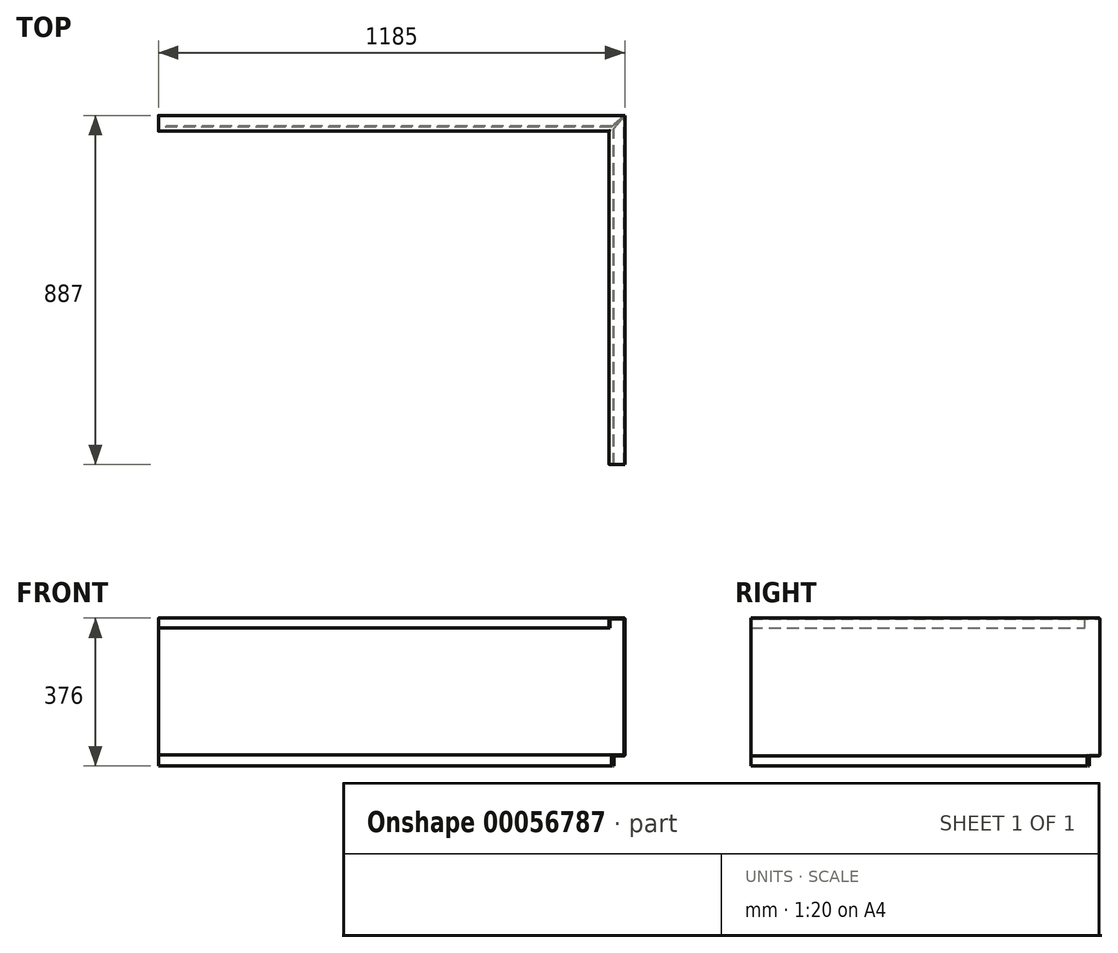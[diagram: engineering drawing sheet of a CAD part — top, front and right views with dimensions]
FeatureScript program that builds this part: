
annotation { "Feature Type Name" : "Feature", "Feature Type Description" : "" }
export const myFeature = defineFeature(function(context is Context, id is Id, definition is map)
    precondition{}
    {
        {
            var Q0;
            Q0=qCreatedBy(makeId("Front.planeOp"),FACE);
            var sketch = newSketch(context, id + "F0", { "sketchPlane" : qUnion([Q0])});
            skLineSegment(sketch, "E0", {"start": v(0, 0) * mm, "end": v(0, -350) * mm});
            skLineSegment(sketch, "E1", {"start": v(0, -350) * mm, "end": v(-27, -350) * mm});
            skLineSegment(sketch, "E2", {"start": v(-27, -350) * mm, "end": v(-27, -376) * mm});
            skLineSegment(sketch, "E3", {"start": v(0, 0) * mm, "end": v(-40, 0) * mm});
            skLineSegment(sketch, "E4", {"start": v(-40, 0) * mm, "end": v(-40, -25) * mm});
            skLineSegment(sketch, "E5.0", {"start": v(-38, -2) * mm, "end": v(-38, -25) * mm});
            skLineSegment(sketch, "E5.1", {"start": v(-29, -348) * mm, "end": v(-29, -376) * mm});
            skLineSegment(sketch, "E5.2", {"start": v(-2, -348) * mm, "end": v(-29, -348) * mm});
            skLineSegment(sketch, "E5.3", {"start": v(-2, -2) * mm, "end": v(-2, -348) * mm});
            skLineSegment(sketch, "E5.4", {"start": v(-2, -2) * mm, "end": v(-38, -2) * mm});
            skLineSegment(sketch, "E6", {"start": v(-40, -25) * mm, "end": v(-38, -25) * mm});
            skLineSegment(sketch, "E7", {"start": v(-29, -376) * mm, "end": v(-27, -376) * mm});
            skSolve(sketch);
        }
        {
            var Q0;
            Q0=qCreatedBy(makeId("Top.planeOp"),FACE);
            var sketch = newSketch(context, id + "F1", { "sketchPlane" : qUnion([Q0])});
            skLineSegment(sketch, "E8", {"start": v(0, 0) * mm, "end": v(0, 887) * mm});
            skLineSegment(sketch, "E9", {"start": v(-1185, 887) * mm, "end": v(0, 887) * mm});
            skSolve(sketch);
        }
        {
            var Q0;
            Q0=qSketchRegion(id+"F0",true);
            var Q1;
            Q1=qConstructionFilter(qBodyType(qCreatedBy(id+"F1",EDGE),BodyType.WIRE),ConstructionObject.NO);
            sweep(context, id + "F2", {"profiles" : qUnion([Q0]), "path" : qUnion([Q1])});
        }
        {
            var Q0;
            Q0=makeQuery(id+"F2.opSweep","SWEPT_FACE",FACE,{"disambiguationData":[OSD([sQuery(id+"F0.wireOp",EDGE,"E5.2"),sQuery(id+"F1.wireOp",EDGE,"E8")])]});
            var sketch = newSketch(context, id + "F3", { "sketchPlane" : qUnion([Q0])});
            skLineSegment(sketch, "E10", {"start": v(-2, 885) * mm, "end": v(-34.18, 858) * mm});
            skLineSegment(sketch, "E11", {"start": v(-34.18, 858) * mm, "end": v(-29, 858) * mm});
            skLineSegment(sketch, "E12", {"start": v(-29, 858) * mm, "end": v(-29, 852.82) * mm});
            skLineSegment(sketch, "E13", {"start": v(-29, 852.82) * mm, "end": v(-2, 885) * mm});
            skSolve(sketch);
        }
        {
            var Q0;
            Q0=makeQuery(id+"F3.imprint","IMPRINT",FACE,{"disambiguationData":[TD([[makeQuery(id+"F3.imprint","IMPRINT",EDGE,{"derivedFrom":sQuery(id+"F3.wireOp",EDGE,"E10")}),1.0]])]});
            extrude(context, id + "F4", {"entities" : qUnion([Q0]), "operationType" : NewBodyOperationType.REMOVE, "oppositeDirection" : true, "depth" : 30 * mm});
        }
        {
            var Q0;
            Q0=makeQuery(id+"F2.opSweep","SWEPT_EDGE",EDGE,{"disambiguationData":[OSD([sQuery(id+"F0.wireOp",EDGE,"E0"),sQuery(id+"F0.wireOp",EDGE,"E3"),sQuery(id+"F1.wireOp",EDGE,"E9")])]});
            var Q1;
            Q1=makeQuery(id+"F2.opSweep","SWEPT_EDGE",EDGE,{"disambiguationData":[OSD([sQuery(id+"F0.wireOp",EDGE,"E3"),sQuery(id+"F0.wireOp",EDGE,"E4"),sQuery(id+"F1.wireOp",EDGE,"E9")])]});
            var Q2;
            Q2=makeQuery(id+"F2.opSweep","SWEPT_EDGE",EDGE,{"disambiguationData":[OSD([sQuery(id+"F0.wireOp",EDGE,"E3"),sQuery(id+"F0.wireOp",EDGE,"E4"),sQuery(id+"F1.wireOp",EDGE,"E8")])]});
            var Q3;
            Q3=makeQuery(id+"F2.opSweep","SWEPT_EDGE",EDGE,{"disambiguationData":[OSD([sQuery(id+"F0.wireOp",EDGE,"E0"),sQuery(id+"F0.wireOp",EDGE,"E3"),sQuery(id+"F1.wireOp",EDGE,"E8")])]});
            var Q4;
            Q4=makeQuery(id+"F2.opSweep","SWEPT_EDGE",EDGE,{"disambiguationData":[OSD([sQuery(id+"F0.wireOp",EDGE,"E0"),sQuery(id+"F0.wireOp",EDGE,"E1"),sQuery(id+"F1.wireOp",EDGE,"E8")])]});
            var Q5;
            Q5=makeQuery(id+"F2.opSweep","SWEPT_EDGE",EDGE,{"disambiguationData":[OSD([sQuery(id+"F0.wireOp",EDGE,"E1"),sQuery(id+"F0.wireOp",EDGE,"E2"),sQuery(id+"F1.wireOp",EDGE,"E8")])]});
            var Q6;
            Q6=makeQuery(id+"F2.opSweep","SWEPT_EDGE",EDGE,{"disambiguationData":[OSD([sQuery(id+"F0.wireOp",EDGE,"E5.1"),sQuery(id+"F0.wireOp",EDGE,"E5.2"),sQuery(id+"F1.wireOp",EDGE,"E9")])]});
            var Q7;
            Q7=makeQuery(id+"F2.opSweep","SWEPT_EDGE",EDGE,{"disambiguationData":[OSD([sQuery(id+"F0.wireOp",EDGE,"E1"),sQuery(id+"F0.wireOp",EDGE,"E2"),sQuery(id+"F1.wireOp",EDGE,"E9")])]});
            var Q8;
            Q8=makeQuery(id+"F2.opSweep","SWEPT_EDGE",EDGE,{"disambiguationData":[OSD([sQuery(id+"F0.wireOp",EDGE,"E0"),sQuery(id+"F0.wireOp",EDGE,"E1"),sQuery(id+"F1.wireOp",EDGE,"E9")])]});
            var Q9;
            Q9=makeQuery(id+"F2.opSweep","SWEPT_EDGE",EDGE,{"disambiguationData":[OSD([sQuery(id+"F0.wireOp",EDGE,"E5.2"),sQuery(id+"F0.wireOp",EDGE,"E5.3"),sQuery(id+"F1.wireOp",EDGE,"E9")])]});
            var Q10;
            Q10=makeQuery(id+"F2.opSweep","SWEPT_EDGE",EDGE,{"disambiguationData":[OSD([sQuery(id+"F0.wireOp",EDGE,"E5.3"),sQuery(id+"F0.wireOp",EDGE,"E5.4"),sQuery(id+"F1.wireOp",EDGE,"E9")])]});
            var Q11;
            Q11=makeQuery(id+"F2.opSweep","SWEPT_EDGE",EDGE,{"disambiguationData":[OSD([sQuery(id+"F0.wireOp",EDGE,"E5.0"),sQuery(id+"F0.wireOp",EDGE,"E5.4"),sQuery(id+"F1.wireOp",EDGE,"E9")])]});
            var Q12;
            Q12=makeQuery(id+"F2.opSweep","SWEPT_EDGE",EDGE,{"disambiguationData":[OSD([sQuery(id+"F0.wireOp",EDGE,"E5.1"),sQuery(id+"F0.wireOp",EDGE,"E5.2"),sQuery(id+"F1.wireOp",EDGE,"E8")])]});
            var Q13;
            Q13=makeQuery(id+"F2.opSweep","SWEPT_EDGE",EDGE,{"disambiguationData":[OSD([sQuery(id+"F0.wireOp",EDGE,"E5.2"),sQuery(id+"F0.wireOp",EDGE,"E5.3"),sQuery(id+"F1.wireOp",EDGE,"E8")])]});
            var Q14;
            Q14=makeQuery(id+"F2.opSweep","SWEPT_EDGE",EDGE,{"disambiguationData":[OSD([sQuery(id+"F0.wireOp",EDGE,"E5.3"),sQuery(id+"F0.wireOp",EDGE,"E5.4"),sQuery(id+"F1.wireOp",EDGE,"E8")])]});
            var Q15;
            Q15=makeQuery(id+"F2.opSweep","SWEPT_EDGE",EDGE,{"disambiguationData":[OSD([sQuery(id+"F0.wireOp",EDGE,"E5.0"),sQuery(id+"F0.wireOp",EDGE,"E5.4"),sQuery(id+"F1.wireOp",EDGE,"E8")])]});
            fillet(context, id + "F5", {"entities" : qUnion([Q0, Q1, Q2, Q3, Q4, Q5, Q6, Q7, Q8, Q9, Q10, Q11, Q12, Q13, Q14, Q15]), "radius" : 2 * mm, "tangentPropagation" : true, "allowEdgeOverflow" : false});
        }
    });
